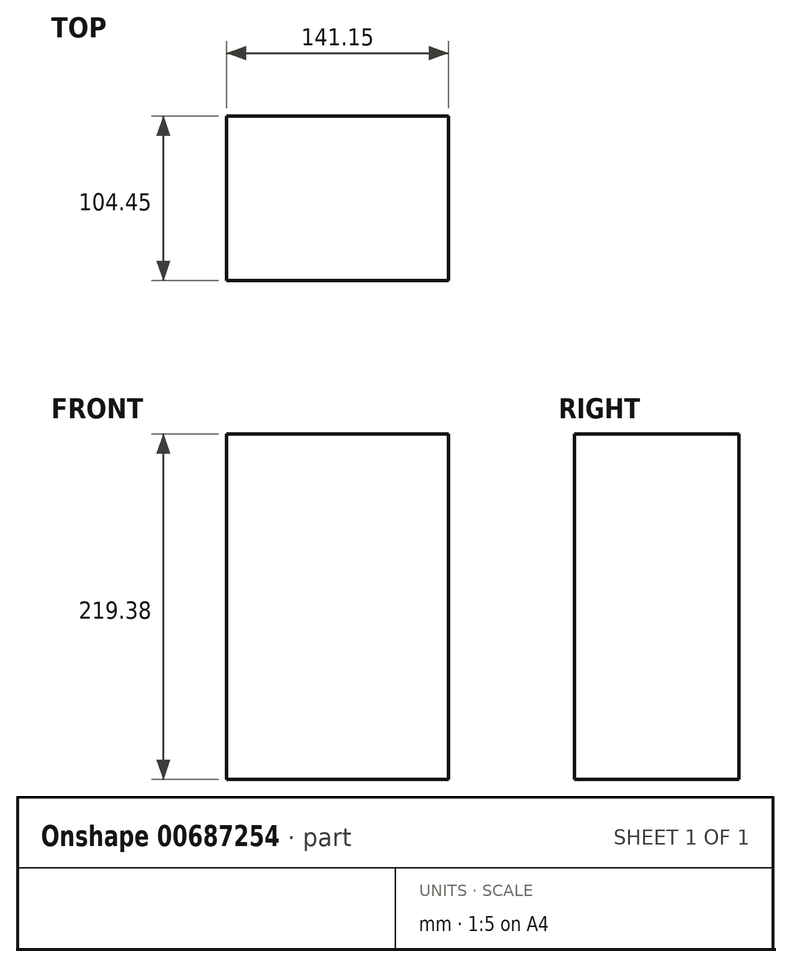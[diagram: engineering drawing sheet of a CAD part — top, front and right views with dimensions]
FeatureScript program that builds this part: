
annotation { "Feature Type Name" : "Feature", "Feature Type Description" : "" }
export const myFeature = defineFeature(function(context is Context, id is Id, definition is map)
    precondition{}
    {
        {
            var Q0;
            Q0=qCreatedBy(makeId("Top.planeOp"),FACE);
            var sketch = newSketch(context, id + "F0", { "sketchPlane" : qUnion([Q0])});
            skLineSegment(sketch, "E0.bottom", {"start": v(0, 0) * mm, "end": v(141.15, 0) * mm});
            skLineSegment(sketch, "E0.top", {"start": v(0, -104.45) * mm, "end": v(141.15, -104.45) * mm});
            skLineSegment(sketch, "E0.left", {"start": v(0, 0) * mm, "end": v(0, -104.45) * mm});
            skLineSegment(sketch, "E0.right", {"start": v(141.15, 0) * mm, "end": v(141.15, -104.45) * mm});
            skSolve(sketch);
        }
        {
            var Q0;
            Q0=makeQuery(id+"F0.imprint","IMPRINT",FACE,{"disambiguationData":[TD([[makeQuery(id+"F0.imprint","IMPRINT",EDGE,{"derivedFrom":sQuery(id+"F0.wireOp",EDGE,"E0.bottom")}),-1.0]])]});
            extrude(context, id + "F1", {"entities" : qUnion([Q0]), "depth" : 219.38 * mm, "offsetDistance" : 25.4 * mm});
        }
    });
